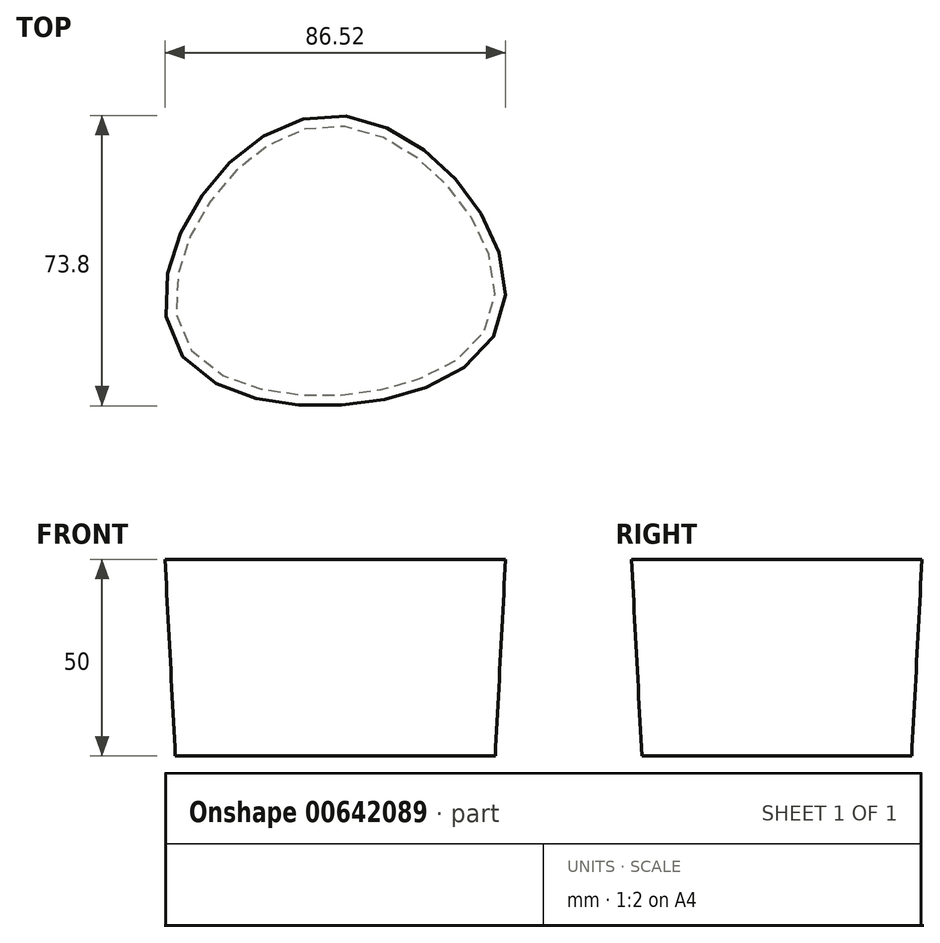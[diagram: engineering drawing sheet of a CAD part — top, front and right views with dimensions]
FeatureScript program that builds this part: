
annotation { "Feature Type Name" : "Feature", "Feature Type Description" : "" }
export const myFeature = defineFeature(function(context is Context, id is Id, definition is map)
    precondition{}
    {
        {
            var Q0;
            Q0=qCreatedBy(makeId("Top.planeOp"),FACE);
            var sketch = newSketch(context, id + "F0", { "sketchPlane" : qUnion([Q0])});
            skFitSpline(sketch, "E0", {"points": [v(0, 29.42) * mm, v(41.2, -21.65) * mm, v(-34.65, -26.7) * mm, v(0, 29.42) * mm]});
            skSolve(sketch);
        }
        {
            var Q0;
            Q0 = qSketchRegion(id + "F0", true);
            extrude(context, id + "F1", {"entities" : qUnion([Q0]), "depth" : 50 * mm, "offsetDistance" : 25.4 * mm, "hasDraft" : true, "draftAngle" : 3 * degree});
        }
        {
            var Q0;
            Q0=makeQuery(id+"F1.opExtrude","CAP_FACE",FACE,{"disambiguationData":[OSD([sQuery(id+"F0.wireOp",EDGE,"E0")])],"isStart":false});
            var sketch = newSketch(context, id + "F2", { "sketchPlane" : qUnion([Q0])});
            skCircle(sketch, "E1", {"center": v(0, 0) * mm, "radius": 17.03 * mm});
            skSolve(sketch);
        }
        {
            var Q0;
            Q0=sQuery(id+"F2.wireOp",EDGE,"E1");
            extrude(context, id + "F3", {"bodyType" : ToolBodyType.SURFACE, "surfaceEntities" : qUnion([Q0]), "depth" : 30 * mm, "offsetDistance" : 25 * mm});
        }
    });
